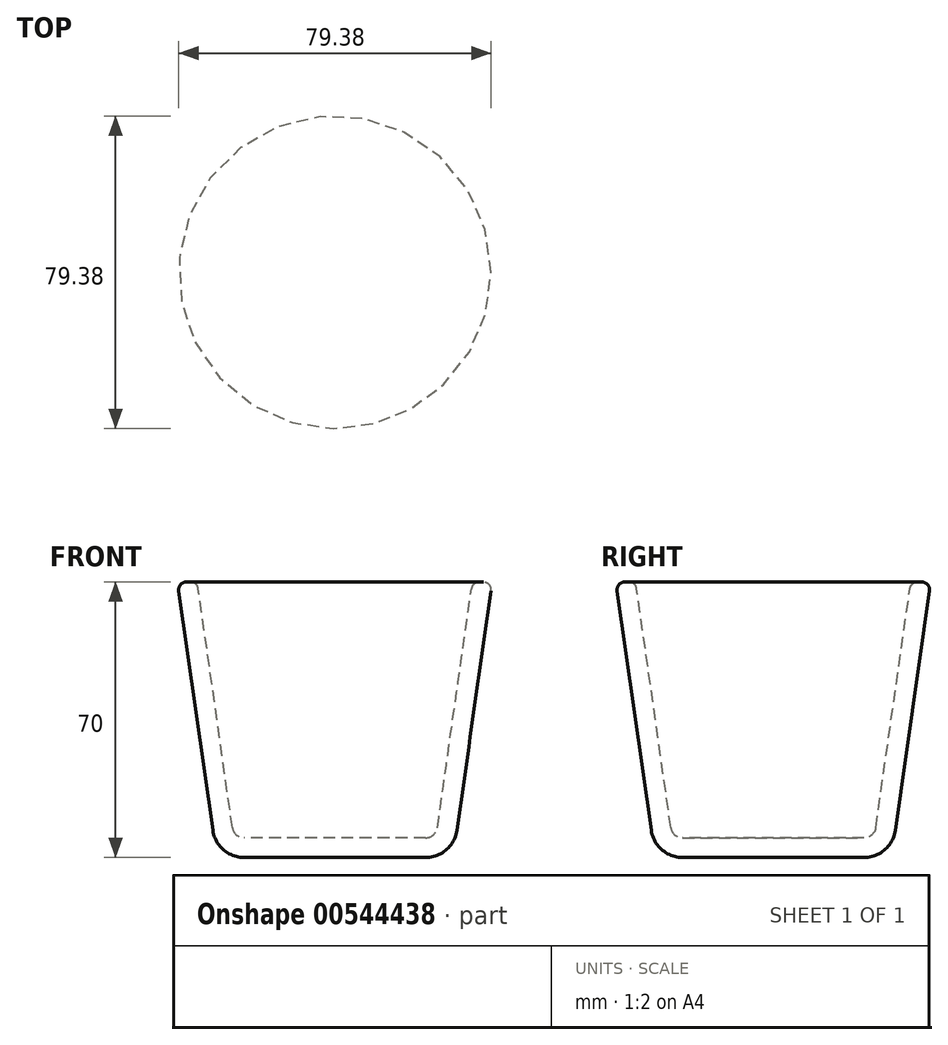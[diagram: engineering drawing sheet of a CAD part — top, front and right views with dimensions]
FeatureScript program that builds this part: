
annotation { "Feature Type Name" : "Feature", "Feature Type Description" : "" }
export const myFeature = defineFeature(function(context is Context, id is Id, definition is map)
    precondition{}
    {
        {
            var Q0;
            Q0=qCreatedBy(makeId("Front.planeOp"),FACE);
            var sketch = newSketch(context, id + "F0", { "sketchPlane" : qUnion([Q0])});
            skLineSegment(sketch, "E0", {"start": v(0, 0) * mm, "end": v(23.06, 0) * mm});
            skLineSegment(sketch, "E1", {"start": v(30.98, 6.87) * mm, "end": v(39.67, 67.72) * mm});
            skPoint(sketch, "E2.visualSharp", {"position": v(30, 0) * mm});
            skArc(sketch, "E2.filletArc", {"start": v(23.06, 0) * mm, "mid": v(28.3, 1.96) * mm, "end": v(30.98, 6.87) * mm});
            skLineSegment(sketch, "E3.0", {"start": v(26.03, 7.58) * mm, "end": v(34.7, 68.28) * mm});
            skLineSegment(sketch, "E4.0", {"start": v(0, 5) * mm, "end": v(23.06, 5) * mm});
            skArc(sketch, "E5.0", {"start": v(23.06, 5) * mm, "mid": v(25.03, 5.73) * mm, "end": v(26.03, 7.58) * mm});
            skLineSegment(sketch, "E6", {"start": v(36.68, 70) * mm, "end": v(37.7, 70) * mm});
            skPoint(sketch, "E7.orphan", {"position": v(31.33, 70) * mm});
            skPoint(sketch, "E8.visualSharp", {"position": v(40, 70) * mm});
            skArc(sketch, "E8.filletArc", {"start": v(39.67, 67.72) * mm, "mid": v(39.2, 69.31) * mm, "end": v(37.7, 70) * mm});
            skPoint(sketch, "E9.visualSharp", {"position": v(34.95, 70) * mm});
            skArc(sketch, "E9.filletArc", {"start": v(36.68, 70) * mm, "mid": v(35.37, 69.51) * mm, "end": v(34.7, 68.28) * mm});
            skLineSegment(sketch, "E10", {"start": v(0, 5) * mm, "end": v(0, 0) * mm});
            skSolve(sketch);
        }
        {
            var Q0;
            Q0=makeQuery(id+"F0.imprint","IMPRINT",FACE,{"disambiguationData":[TD([[makeQuery(id+"F0.imprint","IMPRINT",EDGE,{"derivedFrom":sQuery(id+"F0.wireOp",EDGE,"E0")}),1.0]])]});
            var Q1;
            Q1=sQuery(id+"F0.wireOp",EDGE,"E10");
            revolve(context, id + "F1", {"entities" : qUnion([Q0]), "axis" : qUnion([Q1]), "revolveType" : RevolveType.FULL});
        }
    });
